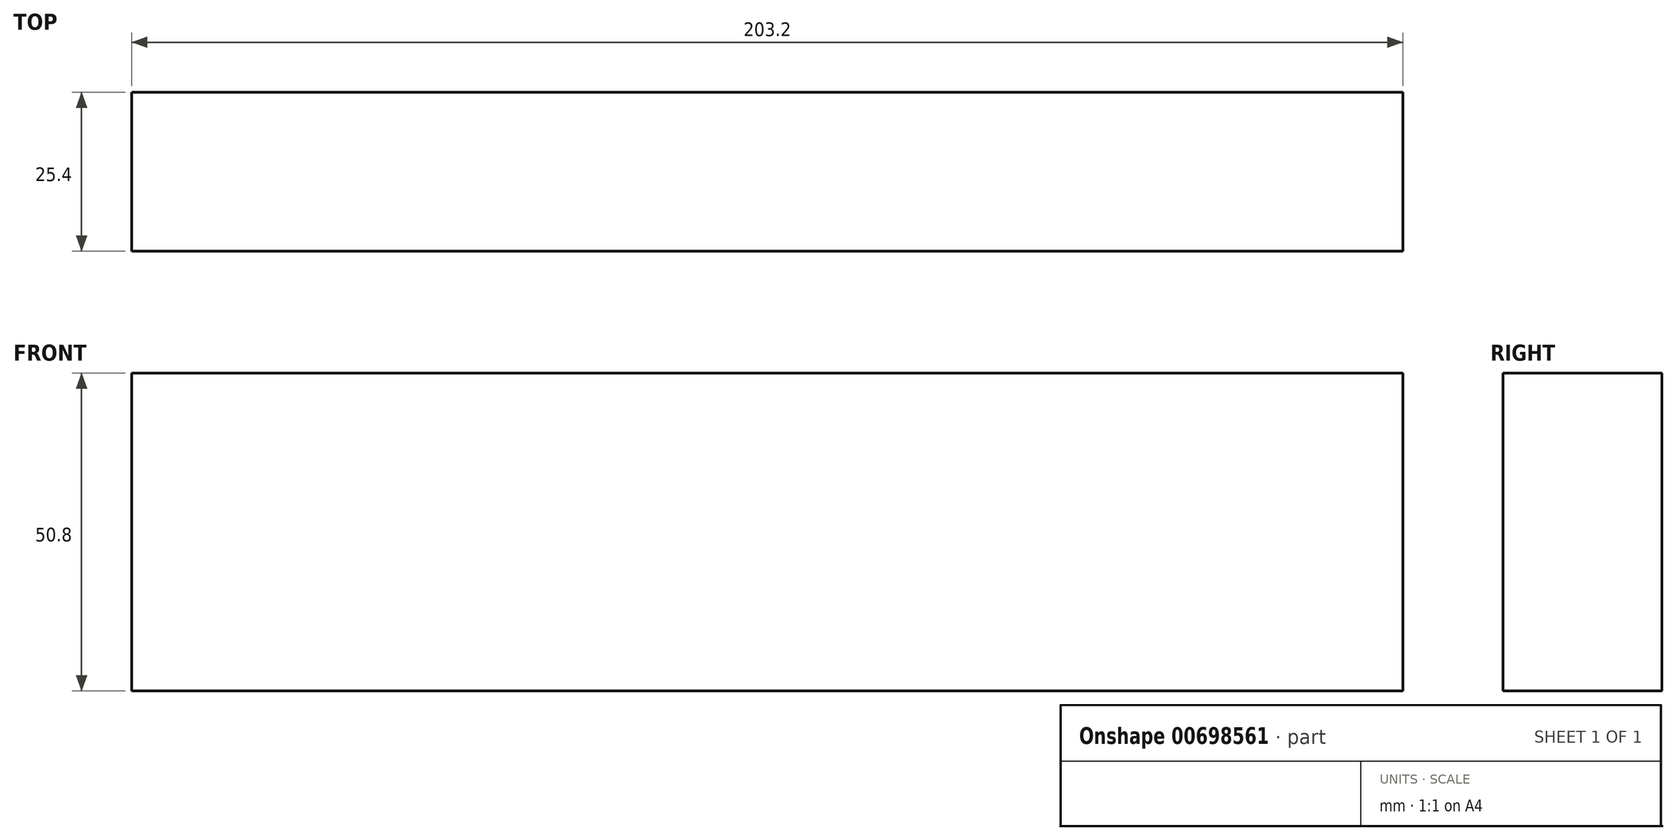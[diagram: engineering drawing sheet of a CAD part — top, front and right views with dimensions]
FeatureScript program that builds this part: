
annotation { "Feature Type Name" : "Feature", "Feature Type Description" : "" }
export const myFeature = defineFeature(function(context is Context, id is Id, definition is map)
    precondition{}
    {
        {
            var Q0;
            Q0=qCreatedBy(makeId("Front.planeOp"),FACE);
            var sketch = newSketch(context, id + "F0", { "sketchPlane" : qUnion([Q0])});
            skLineSegment(sketch, "E0.bottom", {"start": v(-220.64, -233.82) * mm, "end": v(-17.44, -233.82) * mm});
            skLineSegment(sketch, "E0.top", {"start": v(-220.64, -284.62) * mm, "end": v(-17.44, -284.62) * mm});
            skLineSegment(sketch, "E0.left", {"start": v(-220.64, -233.82) * mm, "end": v(-220.64, -284.62) * mm});
            skLineSegment(sketch, "E0.right", {"start": v(-17.44, -233.82) * mm, "end": v(-17.44, -284.62) * mm});
            skSolve(sketch);
        }
        {
            var Q0;
            Q0 = qSketchRegion(id + "F0", true);
            var Q1;
            Q1=makeQuery(id+"F0.imprint","IMPRINT",FACE,{"disambiguationData":[TD([[makeQuery(id+"F0.imprint","IMPRINT",EDGE,{"derivedFrom":sQuery(id+"F0.wireOp",EDGE,"E0.bottom")}),-1.0]])]});
            extrude(context, id + "F1", {"entities" : qUnion([Q0, Q1]), "depth" : 25.4 * mm, "offsetDistance" : 25.4 * mm});
        }
    });
